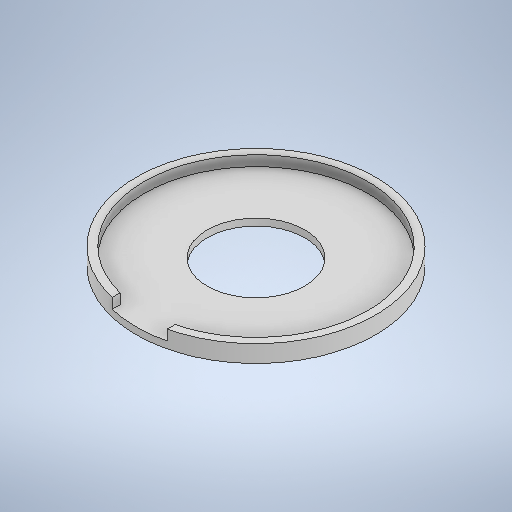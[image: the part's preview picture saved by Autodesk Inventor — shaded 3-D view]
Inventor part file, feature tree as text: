
AUTODESK INVENTOR PART (.ipt)
format: ipt  version: 2025.1 (Build 291241000, 241)  size: 269,312 bytes
history: native  units: mm
features: extrude x4, sketch x4
ambient origin geometry x8: Origin, YZ Plane, XZ Plane, XY Plane, X Axis, Y Axis, Z Axis, Center Point
bodies: Volumenkörper1 (feature_tree)
feature tree (8):
  extrude  "Extrusion1"  Depth=5.0mm TaperAngle=0.0deg
  extrude  "Extrusion2"  Depth=3.0mm TaperAngle=0.0deg
  extrude  "Extrusion3"  TaperAngle=0.0deg  [1 undecoded]
  extrude  "Extrusion4"  Depth=16.0mm
  sketch  "Skizze1"  dims[d0=69.55mm d1=5.0mm d2=0.0mm]
  sketch  "Skizze2"  dims[d3=65.08mm d4=3.0mm d5=0.0mm]
  sketch  "Skizze3"  dims[d6=28.39mm d7=0.0mm d8=0.0mm]
  sketch  "Skizze4"  dims[d9=16.0mm d10=16.0mm d11=10.0mm d12=0.0mm]
note: 1 required parameter value undecoded (feature->parameter linkage not recoverable at this tier; creation-order binding heuristic only, values carry confidence <= 0.55)
